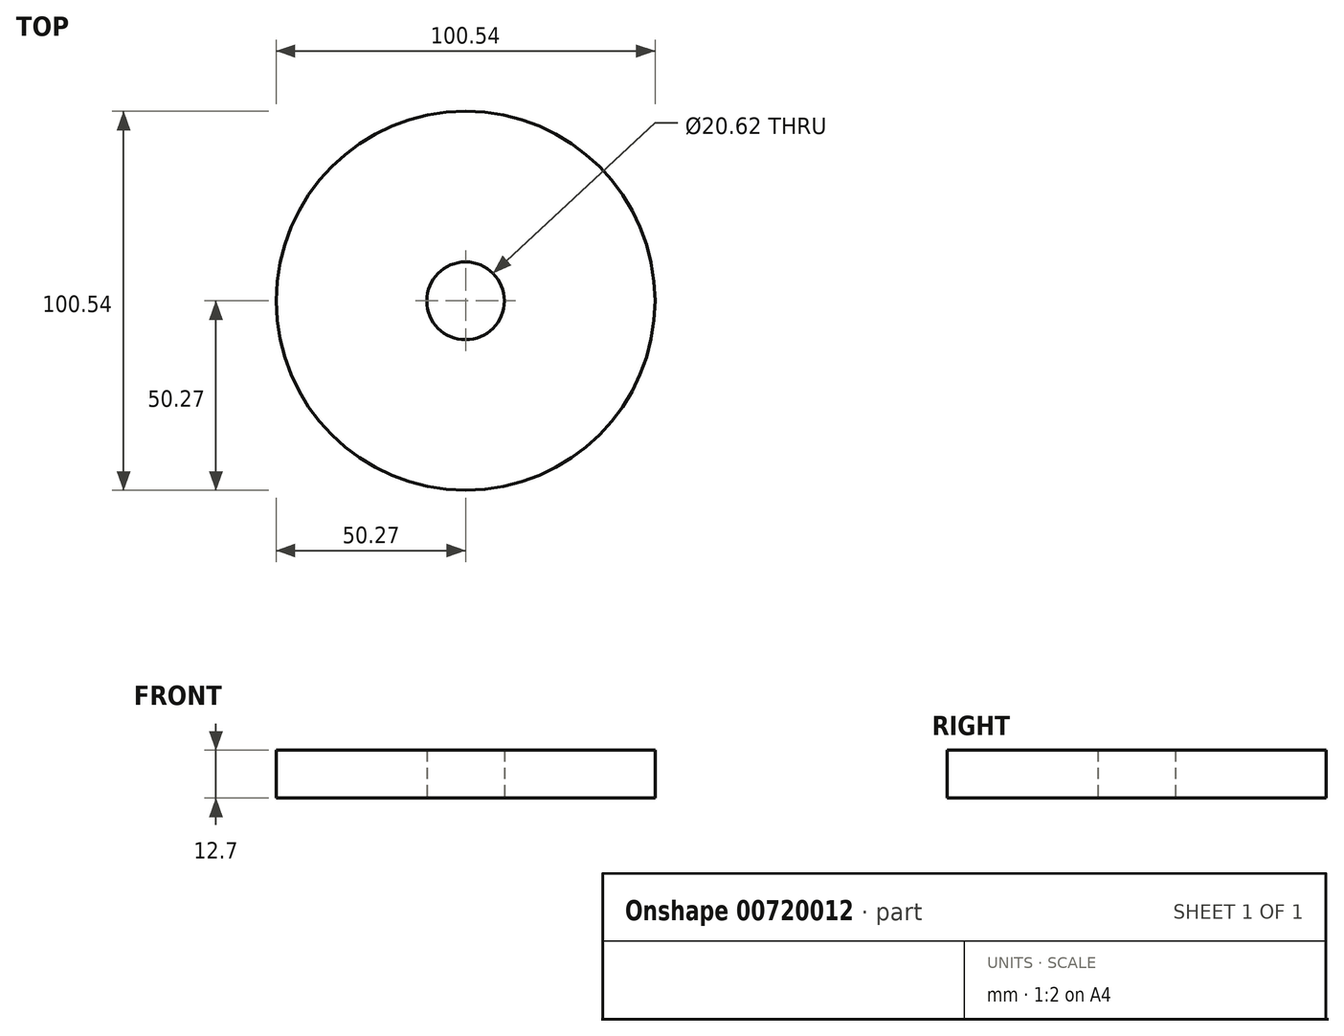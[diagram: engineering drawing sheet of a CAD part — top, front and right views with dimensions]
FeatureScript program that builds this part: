
annotation { "Feature Type Name" : "Feature", "Feature Type Description" : "" }
export const myFeature = defineFeature(function(context is Context, id is Id, definition is map)
    precondition{}
    {
        {
            var Q0;
            Q0=qCreatedBy(makeId("Top.planeOp"),FACE);
            var sketch = newSketch(context, id + "F0", { "sketchPlane" : qUnion([Q0])});
            skCircle(sketch, "E0", {"center": v(0, 0) * mm, "radius": 50.27 * mm});
            skCircle(sketch, "E1", {"center": v(0, 0) * mm, "radius": 10.3 * mm});
            skSolve(sketch);
        }
        {
            var Q0;
            Q0=makeQuery(id+"F0.imprint","IMPRINT",FACE,{"disambiguationData":[TD([[makeQuery(id+"F0.imprint","IMPRINT",EDGE,{"derivedFrom":sQuery(id+"F0.wireOp",EDGE,"E0")}),1.0]])]});
            var Q1;
            Q1=sQuery(id+"F0.wireOp",EDGE,"E0");
            extrude(context, id + "F1", {"entities" : qUnion([Q0]), "surfaceEntities" : qUnion([Q1]), "depth" : 12.7 * mm, "offsetDistance" : 25.4 * mm});
        }
    });
